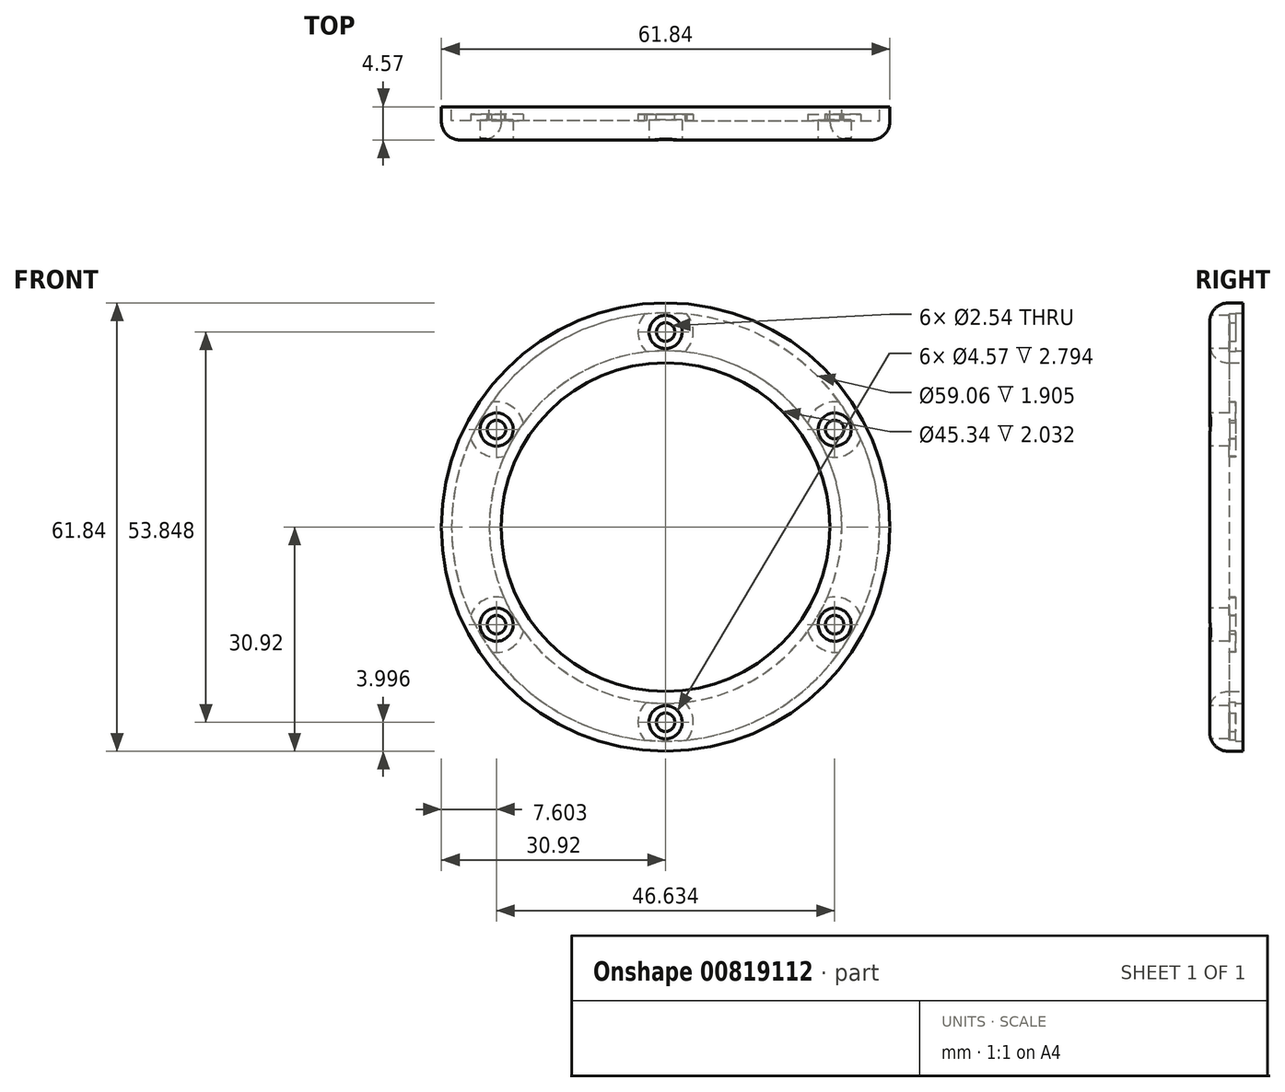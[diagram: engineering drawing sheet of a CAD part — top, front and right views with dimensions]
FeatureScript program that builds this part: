
annotation { "Feature Type Name" : "Feature", "Feature Type Description" : "" }
export const myFeature = defineFeature(function(context is Context, id is Id, definition is map)
    precondition{}
    {
        {
            var Q0;
            Q0=qCreatedBy(makeId("Front.planeOp"),FACE);
            var sketch = newSketch(context, id + "F0", { "sketchPlane" : qUnion([Q0])});
            skCircle(sketch, "E0", {"center": v(0, 0) * mm, "radius": 22.67 * mm});
            skCircle(sketch, "E1", {"center": v(0, 0) * mm, "radius": 30.92 * mm});
            skSolve(sketch);
        }
        {
            var Q0;
            Q0 = qSketchRegion(id + "F0", true);
            extrude(context, id + "F1", {"entities" : qUnion([Q0]), "depth" : 4.57 * mm, "offsetDistance" : 25.4 * mm});
        }
        {
            var Q0;
            Q0=makeQuery(id+"F1.opExtrude","CAP_FACE",FACE,{"disambiguationData":[OSD([sQuery(id+"F0.wireOp",EDGE,"E0"),sQuery(id+"F0.wireOp",EDGE,"E1")])],"isStart":true});
            var sketch = newSketch(context, id + "F2", { "sketchPlane" : qUnion([Q0])});
            skCircle(sketch, "E2", {"center": v(0, 0) * mm, "radius": 24.32 * mm});
            skCircle(sketch, "E3", {"center": v(0, 0) * mm, "radius": 29.53 * mm});
            skCircle(sketch, "E4", {"center": v(0, 0) * mm, "radius": 26.92 * mm, "construction": true});
            skSolve(sketch);
        }
        {
            var Q0;
            Q0 = qSketchRegion(id + "F2", true);
            extrude(context, id + "F3", {"entities" : qUnion([Q0]), "operationType" : NewBodyOperationType.REMOVE, "oppositeDirection" : true, "depth" : 1.9 * mm, "offsetDistance" : 25.4 * mm});
        }
        {
            var Q0;
            Q0=makeQuery(id+"F3.boolean.opBoolean","COPY",FACE,{"derivedFrom":makeQuery(id+"F3.opExtrude","CAP_FACE",FACE,{"disambiguationData":[OSD([sQuery(id+"F2.wireOp",EDGE,"E2"),sQuery(id+"F2.wireOp",EDGE,"E3")])],"isStart":false})});
            var sketch = newSketch(context, id + "F4", { "sketchPlane" : qUnion([Q0])});
            skCircle(sketch, "E5", {"center": v(0, 0) * mm, "radius": 26.92 * mm, "construction": true});
            skCircle(sketch, "E6", {"center": v(0, 26.92) * mm, "radius": 3.81 * mm});
            skCircle(sketch, "E7.1.0", {"center": v(-23.32, 13.46) * mm, "radius": 3.81 * mm});
            skCircle(sketch, "E7.2.0", {"center": v(-23.32, -13.46) * mm, "radius": 3.81 * mm});
            skCircle(sketch, "E7.3.0", {"center": v(0, -26.92) * mm, "radius": 3.81 * mm});
            skCircle(sketch, "E7.4.0", {"center": v(23.32, -13.46) * mm, "radius": 3.81 * mm});
            skCircle(sketch, "E7.5.0", {"center": v(23.32, 13.46) * mm, "radius": 3.81 * mm});
            skSolve(sketch);
        }
        {
            var Q0;
            Q0 = qSketchRegion(id + "F4", true);
            extrude(context, id + "F5", {"entities" : qUnion([Q0]), "operationType" : NewBodyOperationType.ADD, "depth" : 0.89 * mm, "offsetDistance" : 25.4 * mm});
        }
        {
            var Q0;
            Q0=makeQuery(id+"F5.opExtrude","CAP_FACE",FACE,{"disambiguationData":[OSD([sQuery(id+"F4.wireOp",EDGE,"E6")])],"isStart":false});
            var sketch = newSketch(context, id + "F6", { "sketchPlane" : qUnion([Q0])});
            skArc(sketch, "E8.0", {"start": v(-2.9, 29.38) * mm, "mid": v(-3.8, 26.73) * mm, "end": v(-2.64, 24.18) * mm, "construction": true});
            skArc(sketch, "E9.0", {"start": v(2.64, 24.18) * mm, "mid": v(3.8, 26.73) * mm, "end": v(2.9, 29.38) * mm, "construction": true});
            skCircle(sketch, "E10", {"center": v(0, 26.92) * mm, "radius": 1.27 * mm});
            skCircle(sketch, "E11.1.0", {"center": v(-23.32, 13.46) * mm, "radius": 1.27 * mm});
            skCircle(sketch, "E11.2.0", {"center": v(-23.32, -13.46) * mm, "radius": 1.27 * mm});
            skCircle(sketch, "E11.3.0", {"center": v(0, -26.92) * mm, "radius": 1.27 * mm});
            skCircle(sketch, "E11.4.0", {"center": v(23.32, -13.46) * mm, "radius": 1.27 * mm});
            skCircle(sketch, "E11.5.0", {"center": v(23.32, 13.46) * mm, "radius": 1.27 * mm});
            skPoint(sketch, "E11.center", {"position": v(0, 0) * mm});
            skSolve(sketch);
        }
        {
            var Q0;
            Q0 = qSketchRegion(id + "F6", true);
            extrude(context, id + "F7", {"entities" : qUnion([Q0]), "operationType" : NewBodyOperationType.REMOVE, "endBound" : BoundingType.THROUGH_ALL, "oppositeDirection" : true, "depth" : 25.4 * mm, "offsetDistance" : 25.4 * mm});
        }
        {
            var Q0;
            Q0=makeQuery(id+"F1.opExtrude","CAP_FACE",FACE,{"disambiguationData":[OSD([sQuery(id+"F0.wireOp",EDGE,"E0"),sQuery(id+"F0.wireOp",EDGE,"E1")])],"isStart":false});
            var sketch = newSketch(context, id + "F8", { "sketchPlane" : qUnion([Q0])});
            skCircle(sketch, "E12.0", {"center": v(0, 26.92) * mm, "radius": 1.27 * mm, "construction": true});
            skCircle(sketch, "E13", {"center": v(0, 26.92) * mm, "radius": 2.29 * mm});
            skCircle(sketch, "E14.1.0", {"center": v(-23.32, 13.46) * mm, "radius": 2.29 * mm});
            skCircle(sketch, "E14.2.0", {"center": v(-23.32, -13.46) * mm, "radius": 2.29 * mm});
            skCircle(sketch, "E14.3.0", {"center": v(0, -26.92) * mm, "radius": 2.29 * mm});
            skCircle(sketch, "E14.4.0", {"center": v(23.32, -13.46) * mm, "radius": 2.29 * mm});
            skCircle(sketch, "E14.5.0", {"center": v(23.32, 13.46) * mm, "radius": 2.29 * mm});
            skPoint(sketch, "E14.center", {"position": v(0, 0) * mm});
            skSolve(sketch);
        }
        {
            var Q0;
            Q0 = qSketchRegion(id + "F8", true);
            extrude(context, id + "F9", {"entities" : qUnion([Q0]), "operationType" : NewBodyOperationType.REMOVE, "oppositeDirection" : true, "depth" : 2.8 * mm, "offsetDistance" : 25.4 * mm});
        }
        {
            var Q0;
            Q0=makeQuery(id+"F1.opExtrude","CAP_EDGE",EDGE,{"disambiguationData":[OSD([sQuery(id+"F0.wireOp",EDGE,"E1")])],"isStart":false});
            var Q1;
            Q1=makeQuery(id+"F1.opExtrude","CAP_EDGE",EDGE,{"disambiguationData":[OSD([sQuery(id+"F0.wireOp",EDGE,"E0")])],"isStart":false});
            fillet(context, id + "F10", {"entities" : qUnion([Q0, Q1]), "radius" : 2.54 * mm, "tangentPropagation" : true, "allowEdgeOverflow" : false});
        }
    });
